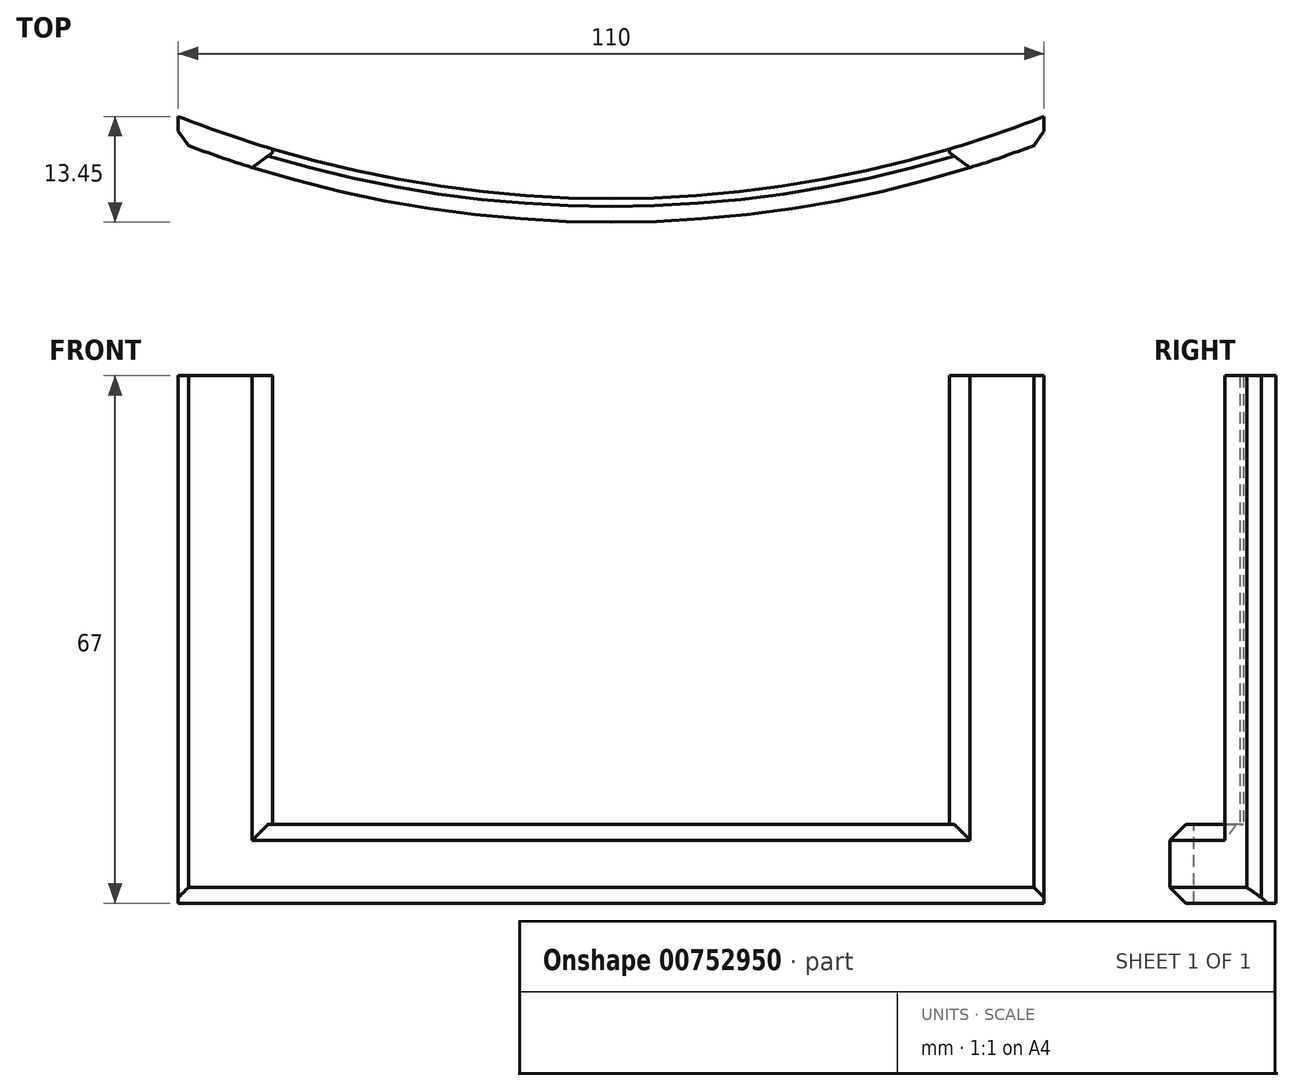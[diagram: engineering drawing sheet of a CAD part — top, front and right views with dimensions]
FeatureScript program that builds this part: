
annotation { "Feature Type Name" : "Feature", "Feature Type Description" : "" }
export const myFeature = defineFeature(function(context is Context, id is Id, definition is map)
    precondition{}
    {
        {
            var Q0;
            Q0=qCreatedBy(makeId("Top.planeOp"),FACE);
            var sketch = newSketch(context, id + "F0", { "sketchPlane" : qUnion([Q0])});
            skArc(sketch, "E0", {"start": v(-55, 10.45) * mm, "mid": v(0, 0) * mm, "end": v(55, 10.45) * mm});
            skArc(sketch, "E1", {"start": v(-55, 7.23) * mm, "mid": v(0, -3) * mm, "end": v(55, 7.23) * mm});
            skLineSegment(sketch, "E2.top", {"start": v(43, 14.3) * mm, "end": v(-43, 14.3) * mm});
            skLineSegment(sketch, "E2.left", {"start": v(43, 3.17) * mm, "end": v(43, 14.3) * mm});
            skLineSegment(sketch, "E2.right", {"start": v(-43, 3.17) * mm, "end": v(-43, 14.3) * mm});
            skPoint(sketch, "E2.middle", {"position": v(0, -18.34) * mm});
            skPoint(sketch, "E2.bottom.end.orphan", {"position": v(-43, -50.97) * mm});
            skPoint(sketch, "E3.orphan", {"position": v(43, -50.97) * mm});
            skLineSegment(sketch, "E4.left", {"start": v(55, 10.45) * mm, "end": v(55, 7.23) * mm});
            skLineSegment(sketch, "E4.right", {"start": v(-55, 10.45) * mm, "end": v(-55, 7.23) * mm});
            skPoint(sketch, "E4.middle", {"position": v(0, 0) * mm});
            skPoint(sketch, "E5.orphan", {"position": v(-55, 19.42) * mm});
            skPoint(sketch, "E6.orphan", {"position": v(55, 19.42) * mm});
            skPoint(sketch, "E4.top.start.orphan", {"position": v(55, -19.42) * mm});
            skPoint(sketch, "E7.orphan", {"position": v(-55, -19.42) * mm});
            skPoint(sketch, "E8", {"position": v(-43, 6.3) * mm});
            skSolve(sketch);
        }
        {
            var Q0;
            {var subQ0=sQuery(id+"F0.wireOp",EDGE,"E4.right");Q0=makeQuery(id+"F0.imprint","IMPRINT",FACE,{"disambiguationData":[TD([[makeQuery(id+"F0.imprint","IMPRINT",EDGE,{"derivedFrom":subQ0}),1.0]])]});}
            var Q1;
            {var subQ0=sQuery(id+"F0.wireOp",EDGE,"E4.left");Q1=makeQuery(id+"F0.imprint","IMPRINT",FACE,{"disambiguationData":[TD([[makeQuery(id+"F0.imprint","IMPRINT",EDGE,{"derivedFrom":subQ0}),-1.0]])]});}
            var Q2;
            {var subQ0=sQuery(id+"F0.wireOp",EDGE,"E2.right");var subQ1=sQuery(id+"F0.wireOp",EDGE,"E0");var subQ2=makeQuery(id+"F0.imprint","INTERSECT",VERTEX,{"derivedFrom":[subQ1,subQ0]});Q2=makeQuery(id+"F0.imprint","IMPRINT",FACE,{"disambiguationData":[TD([[makeQuery(id+"F0.imprint","IMPRINT",EDGE,{"disambiguationData":[TD([[subQ2,-1.0]])],"derivedFrom":subQ1}),-1.0]])]});}
            extrude(context, id + "F1", {"entities" : qUnion([Q0, Q1, Q2]), "oppositeDirection" : true, "depth" : 10 * mm, "offsetDistance" : 25 * mm});
        }
        {
            var Q0;
            {var subQ0=sQuery(id+"F0.wireOp",EDGE,"E4.right");Q0=makeQuery(id+"F0.imprint","IMPRINT",FACE,{"disambiguationData":[TD([[makeQuery(id+"F0.imprint","IMPRINT",EDGE,{"derivedFrom":subQ0}),1.0]])]});}
            var Q1;
            {var subQ0=sQuery(id+"F0.wireOp",EDGE,"E4.left");Q1=makeQuery(id+"F0.imprint","IMPRINT",FACE,{"disambiguationData":[TD([[makeQuery(id+"F0.imprint","IMPRINT",EDGE,{"derivedFrom":subQ0}),-1.0]])]});}
            extrude(context, id + "F2", {"entities" : qUnion([Q0, Q1]), "operationType" : NewBodyOperationType.ADD, "depth" : 57 * mm, "offsetDistance" : 25 * mm});
        }
        {
            var Q0;
            Q0=makeQuery(id+"F2.opExtrude","SWEPT_EDGE",EDGE,{"disambiguationData":[OSD([sQuery(id+"F0.wireOp",EDGE,"E1"),sQuery(id+"F0.wireOp",EDGE,"E2.right")])]});
            var Q1;
            Q1=makeQuery(id+"F1.opExtrude","CAP_EDGE",EDGE,{"disambiguationData":[OSD([sQuery(id+"F0.wireOp",EDGE,"E1")])],"isStart":true});
            var Q2;
            Q2=makeQuery(id+"F2.opExtrude","SWEPT_EDGE",EDGE,{"disambiguationData":[OSD([sQuery(id+"F0.wireOp",EDGE,"E1"),sQuery(id+"F0.wireOp",EDGE,"E2.left")])]});
            var Q3;
            {var subQ0=sQuery(id+"F0.wireOp",EDGE,"E4.left");var subQ1=sQuery(id+"F0.wireOp",EDGE,"E1");Q3=makeQuery(id+"F2.boolean.opBoolean","MERGE",EDGE,{"derivedFrom":[makeQuery(id+"F1.opExtrude","SWEPT_EDGE",EDGE,{"disambiguationData":[OSD([subQ1,subQ0])]}),makeQuery(id+"F2.opExtrude","SWEPT_EDGE",EDGE,{"disambiguationData":[OSD([subQ1,subQ0])]})]});}
            var Q4;
            Q4=makeQuery(id+"F1.opExtrude","CAP_EDGE",EDGE,{"disambiguationData":[OSD([sQuery(id+"F0.wireOp",EDGE,"E1")])],"isStart":false});
            var Q5;
            {var subQ0=sQuery(id+"F0.wireOp",EDGE,"E4.right");var subQ1=sQuery(id+"F0.wireOp",EDGE,"E1");Q5=makeQuery(id+"F2.boolean.opBoolean","MERGE",EDGE,{"derivedFrom":[makeQuery(id+"F1.opExtrude","SWEPT_EDGE",EDGE,{"disambiguationData":[OSD([subQ1,subQ0])]}),makeQuery(id+"F2.opExtrude","SWEPT_EDGE",EDGE,{"disambiguationData":[OSD([subQ1,subQ0])]})]});}
            chamfer(context, id + "F3", {"entities" : qUnion([Q0, Q1, Q2, Q3, Q4, Q5]), "width" : 2 * mm, "tangentPropagation" : true});
        }
    });
